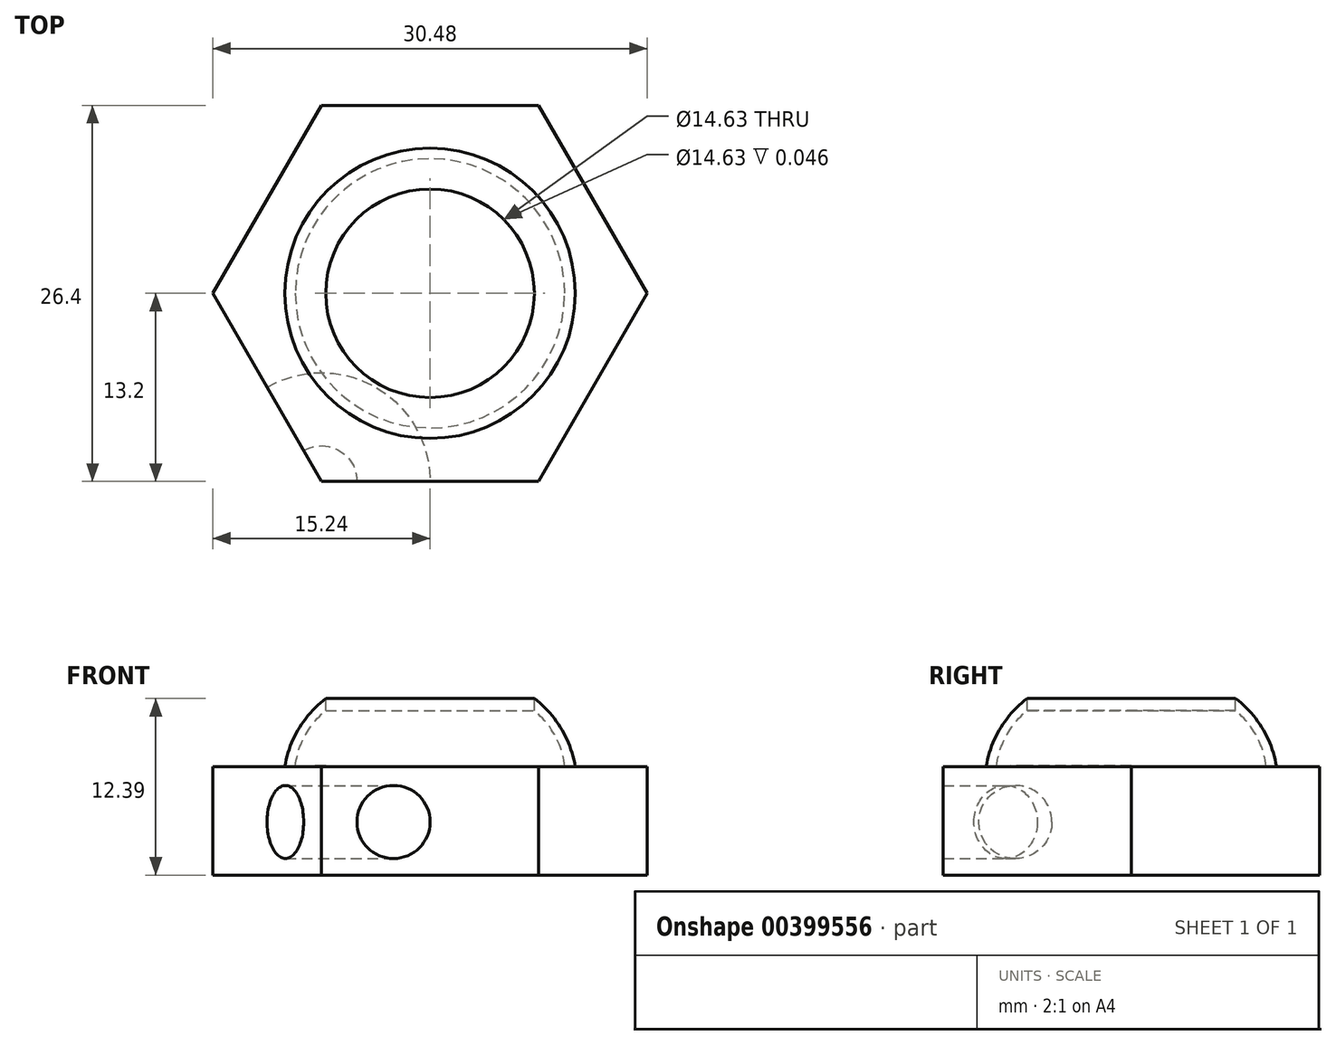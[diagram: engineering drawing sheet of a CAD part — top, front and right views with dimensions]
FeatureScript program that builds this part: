
annotation { "Feature Type Name" : "Feature", "Feature Type Description" : "" }
export const myFeature = defineFeature(function(context is Context, id is Id, definition is map)
    precondition{}
    {
        {
            var Q0;
            Q0=qCreatedBy(makeId("Top.planeOp"),FACE);
            var sketch = newSketch(context, id + "F0", { "sketchPlane" : qUnion([Q0])});
            skCircle(sketch, "E0.cCircle", {"center": v(0, 0) * mm, "radius": 13.2 * mm, "construction": true});
            skLineSegment(sketch, "E0.0", {"start": v(15.24, 0) * mm, "end": v(7.62, -13.2) * mm});
            skLineSegment(sketch, "E0.1", {"start": v(7.62, -13.2) * mm, "end": v(-7.62, -13.2) * mm});
            skLineSegment(sketch, "E0.2", {"start": v(-7.62, -13.2) * mm, "end": v(-15.24, 0) * mm});
            skLineSegment(sketch, "E0.3", {"start": v(-15.24, 0) * mm, "end": v(-7.62, 13.2) * mm});
            skLineSegment(sketch, "E0.4", {"start": v(-7.62, 13.2) * mm, "end": v(7.62, 13.2) * mm});
            skLineSegment(sketch, "E0.5", {"start": v(7.62, 13.2) * mm, "end": v(15.24, 0) * mm});
            skPoint(sketch, "E0.0.midPoint", {"position": v(11.43, -6.6) * mm});
            skSolve(sketch);
        }
        {
            var Q0;
            Q0=makeQuery(id+"F0.imprint","IMPRINT",FACE,{"disambiguationData":[TD([[makeQuery(id+"F0.imprint","IMPRINT",EDGE,{"derivedFrom":sQuery(id+"F0.wireOp",EDGE,"E0.0")}),-1.0]])]});
            extrude(context, id + "F1", {"entities" : qUnion([Q0]), "depth" : 7.62 * mm});
        }
        {
            var Q0;
            Q0=makeQuery(id+"F1.opExtrude","CAP_FACE",FACE,{"disambiguationData":[OSD([sQuery(id+"F0.wireOp",EDGE,"E0.0"),sQuery(id+"F0.wireOp",EDGE,"E0.1"),sQuery(id+"F0.wireOp",EDGE,"E0.2"),sQuery(id+"F0.wireOp",EDGE,"E0.3"),sQuery(id+"F0.wireOp",EDGE,"E0.4"),sQuery(id+"F0.wireOp",EDGE,"E0.5")])],"isStart":false});
            var sketch = newSketch(context, id + "F2", { "sketchPlane" : qUnion([Q0])});
            skCircle(sketch, "E1", {"center": v(0, 0) * mm, "radius": 10.19 * mm});
            skSolve(sketch);
        }
        {
            var Q0;
            Q0 = qSketchRegion(id + "F2", true);
            extrude(context, id + "F3", {"entities" : qUnion([Q0]), "operationType" : NewBodyOperationType.ADD, "depth" : 6.35 * mm});
        }
        {
            var Q0;
            Q0=makeQuery(id+"F3.opExtrude","CAP_EDGE",EDGE,{"disambiguationData":[OSD([sQuery(id+"F2.wireOp",EDGE,"E1")])],"isStart":false});
            fillet(context, id + "F4", {"entities" : qUnion([Q0]), "radius" : 7.62 * mm, "tangentPropagation" : true, "allowEdgeOverflow" : false});
        }
        {
            var Q0;
            Q0=makeQuery(id+"F3.opExtrude","CAP_FACE",FACE,{"disambiguationData":[OSD([sQuery(id+"F2.wireOp",EDGE,"E1")])],"isStart":false});
            var sketch = newSketch(context, id + "F5", { "sketchPlane" : qUnion([Q0])});
            skCircle(sketch, "E2", {"center": v(0, 0) * mm, "radius": 7.32 * mm});
            skSolve(sketch);
        }
        {
            var Q0;
            Q0 = qSketchRegion(id + "F5", true);
            var Q1;
            Q1=makeQuery(id+"F1.opExtrude","CAP_FACE",FACE,{"disambiguationData":[OSD([sQuery(id+"F0.wireOp",EDGE,"E0.0"),sQuery(id+"F0.wireOp",EDGE,"E0.1"),sQuery(id+"F0.wireOp",EDGE,"E0.2"),sQuery(id+"F0.wireOp",EDGE,"E0.3"),sQuery(id+"F0.wireOp",EDGE,"E0.4"),sQuery(id+"F0.wireOp",EDGE,"E0.5")])],"isStart":false});
            extrude(context, id + "F6", {"entities" : qUnion([Q0]), "operationType" : NewBodyOperationType.REMOVE, "endBound" : BoundingType.UP_TO_SURFACE, "oppositeDirection" : true, "endBoundEntityFace" : qUnion([Q1]), "depth" : 6.1 * mm});
        }
        {
            var Q0;
            Q0=qCreatedBy(makeId("Front.planeOp"),FACE);
            var sketch = newSketch(context, id + "F7", { "sketchPlane" : qUnion([Q0])});
            skArc(sketch, "E3", {"start": v(9.45, 7.64) * mm, "mid": v(8.74, 9.84) * mm, "end": v(7.24, 11.6) * mm});
            skLineSegment(sketch, "E4", {"start": v(7.24, 11.6) * mm, "end": v(7.24, 7.67) * mm});
            skLineSegment(sketch, "E5", {"start": v(7.24, 7.67) * mm, "end": v(9.45, 7.64) * mm});
            skSolve(sketch);
        }
        {
            var Q0;
            Q0 = qSketchRegion(id + "F7", true);
            var Q1;
            Q1=makeQuery(id+"F6.boolean.opBoolean","COPY",FACE,{"derivedFrom":makeQuery(id+"F6.opExtrude","SWEPT_FACE",FACE,{"disambiguationData":[OSD([sQuery(id+"F5.wireOp",EDGE,"E2")])]})});
            revolve(context, id + "F8", {"operationType" : NewBodyOperationType.REMOVE, "entities" : qUnion([Q0]), "axis" : qUnion([Q1]), "revolveType" : RevolveType.FULL});
        }
        {
            var Q0;
            Q0=makeQuery(id+"F1.opExtrude","SWEPT_FACE",FACE,{"disambiguationData":[OSD([sQuery(id+"F0.wireOp",EDGE,"E0.1")])]});
            var sketch = newSketch(context, id + "F9", { "sketchPlane" : qUnion([Q0])});
            skCircle(sketch, "E6", {"center": v(-2.56, 3.72) * mm, "radius": 2.57 * mm});
            skSolve(sketch);
        }
        {
            var Q0;
            Q0 = qSketchRegion(id + "F9", true);
            var Q1;
            Q1=makeQuery(id+"F1.opExtrude","SWEPT_EDGE",EDGE,{"disambiguationData":[OSD([sQuery(id+"F0.wireOp",EDGE,"E0.1"),sQuery(id+"F0.wireOp",EDGE,"E0.2")])]});
            revolve(context, id + "F10", {"operationType" : NewBodyOperationType.REMOVE, "entities" : qUnion([Q0]), "axis" : qUnion([Q1]), "revolveType" : RevolveType.FULL, "oppositeDirection" : true});
        }
    });
